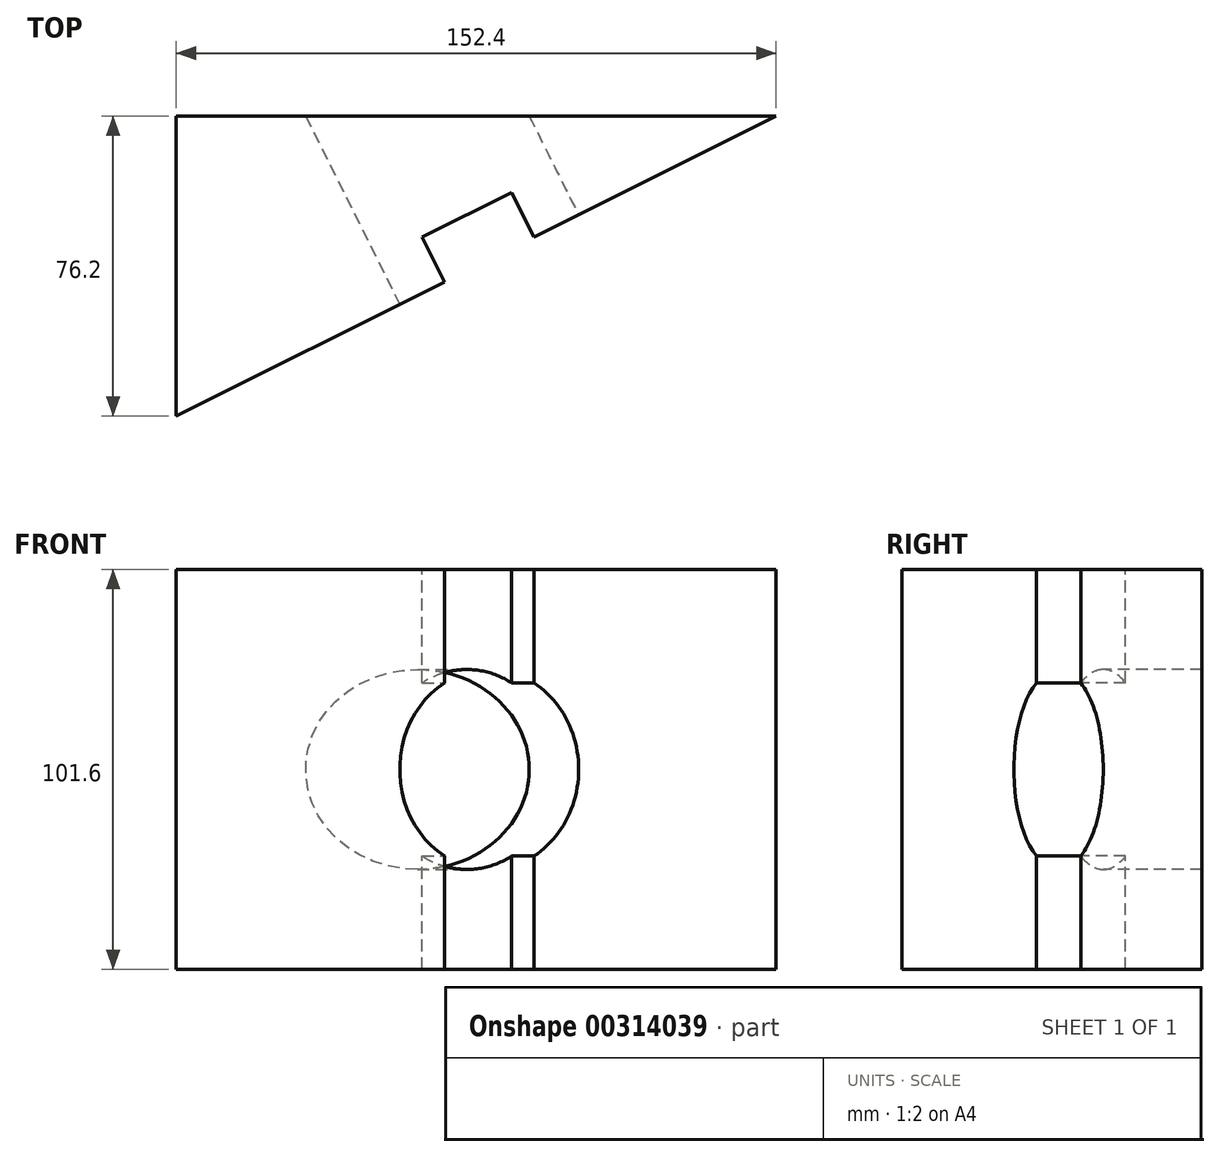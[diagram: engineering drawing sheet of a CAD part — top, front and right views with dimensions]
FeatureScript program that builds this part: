
annotation { "Feature Type Name" : "Feature", "Feature Type Description" : "" }
export const myFeature = defineFeature(function(context is Context, id is Id, definition is map)
    precondition{}
    {
        {
            var Q0;
            Q0=qCreatedBy(makeId("Top.planeOp"),FACE);
            var sketch = newSketch(context, id + "F0", { "sketchPlane" : qUnion([Q0])});
            skLineSegment(sketch, "E0.bottom", {"start": v(0, 0) * mm, "end": v(152.4, 0) * mm});
            skLineSegment(sketch, "E0.top", {"start": v(0, -76.2) * mm, "end": v(152.4, -76.2) * mm});
            skLineSegment(sketch, "E0.left", {"start": v(0, 0) * mm, "end": v(0, -76.2) * mm});
            skLineSegment(sketch, "E0.right", {"start": v(152.4, 0) * mm, "end": v(152.4, -76.2) * mm});
            skLineSegment(sketch, "E1", {"start": v(152.4, 0) * mm, "end": v(0, -76.2) * mm});
            skSolve(sketch);
        }
        {
            var Q0;
            Q0=makeQuery(id+"F0.imprint","IMPRINT",FACE,{"disambiguationData":[TD([[makeQuery(id+"F0.imprint","IMPRINT",EDGE,{"derivedFrom":sQuery(id+"F0.wireOp",EDGE,"E0.bottom")}),-1.0]])]});
            extrude(context, id + "F1", {"entities" : qUnion([Q0]), "depth" : 101.6 * mm});
        }
        {
            var Q0;
            Q0=makeQuery(id+"F1.opExtrude","SWEPT_FACE",FACE,{"disambiguationData":[OSD([sQuery(id+"F0.wireOp",EDGE,"E1")])]});
            var sketch = newSketch(context, id + "F2", { "sketchPlane" : qUnion([Q0])});
            skLineSegment(sketch, "E2.bottom", {"start": v(67.52, 0) * mm, "end": v(42.12, 0) * mm});
            skLineSegment(sketch, "E2.top", {"start": v(67.52, 101.6) * mm, "end": v(42.12, 101.6) * mm});
            skLineSegment(sketch, "E2.left", {"start": v(67.52, 0) * mm, "end": v(67.52, 101.6) * mm});
            skLineSegment(sketch, "E2.right", {"start": v(42.12, 0) * mm, "end": v(42.12, 101.6) * mm});
            skPoint(sketch, "E2.middle", {"position": v(54.82, 50.8) * mm});
            skSolve(sketch);
        }
        {
            var Q0;
            Q0=makeQuery(id+"F2.imprint","IMPRINT",FACE,{"disambiguationData":[TD([[makeQuery(id+"F2.imprint","IMPRINT",EDGE,{"derivedFrom":sQuery(id+"F2.wireOp",EDGE,"E2.bottom")}),-1.0]])]});
            extrude(context, id + "F3", {"entities" : qUnion([Q0]), "operationType" : NewBodyOperationType.REMOVE, "oppositeDirection" : true, "depth" : 12.7 * mm});
        }
        {
            var Q0;
            {var subQ0=sQuery(id+"F0.wireOp",EDGE,"E0.bottom");var subQ1=sQuery(id+"F0.wireOp",EDGE,"E1");Q0=makeQuery(id+"F3.boolean.opBoolean","SPLIT",FACE,{"disambiguationData":[TD([makeQuery(id+"F1.opExtrude","SWEPT_FACE",FACE,{"disambiguationData":[OSD([subQ0])]})])],"derivedFrom":makeQuery(id+"F1.opExtrude","SWEPT_FACE",FACE,{"disambiguationData":[OSD([subQ1])]})});}
            var sketch = newSketch(context, id + "F4", { "sketchPlane" : qUnion([Q0])});
            skCircle(sketch, "E3", {"center": v(54.82, 50.8) * mm, "radius": 25.4 * mm});
            skSolve(sketch);
        }
        {
            var Q0;
            Q0 = qSketchRegion(id + "F4", true);
            extrude(context, id + "F5", {"entities" : qUnion([Q0]), "operationType" : NewBodyOperationType.ADD, "depth" : 25.4 * mm});
        }
        {
            var Q0;
            Q0=makeQuery(id+"F5.opExtrude","CAP_FACE",FACE,{"disambiguationData":[OSD([sQuery(id+"F4.wireOp",EDGE,"E3")])],"isStart":false});
            extrude(context, id + "F6", {"entities" : qUnion([Q0]), "operationType" : NewBodyOperationType.REMOVE, "oppositeDirection" : true, "depth" : 192.79 * mm});
        }
    });
